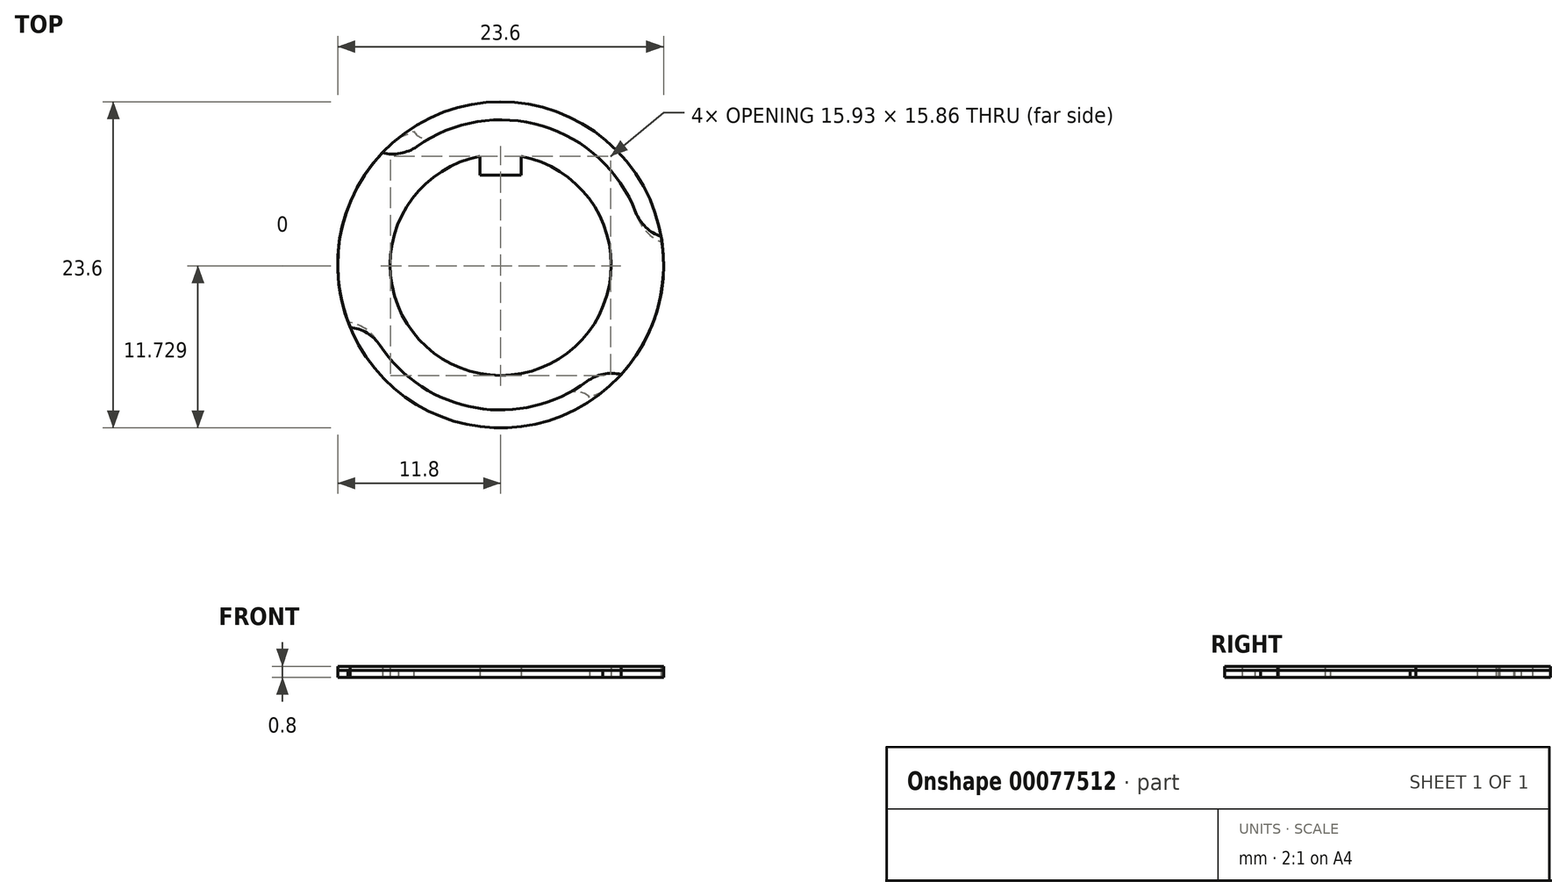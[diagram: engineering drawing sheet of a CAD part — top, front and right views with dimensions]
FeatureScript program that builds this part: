
annotation { "Feature Type Name" : "Feature", "Feature Type Description" : "" }
export const myFeature = defineFeature(function(context is Context, id is Id, definition is map)
    precondition{}
    {
        {
            var Q0;
            Q0=qCreatedBy(makeId("Top.planeOp"),FACE);
            var sketch = newSketch(context, id + "F0", { "sketchPlane" : qUnion([Q0])});
            skArc(sketch, "E0", {"start": v(7.4, -9.19) * mm, "mid": v(3.12, 11.38) * mm, "end": v(-11.05, -4.13) * mm});
            skArc(sketch, "E1", {"start": v(-1.5, 7.86) * mm, "mid": v(0, -8) * mm, "end": v(1.5, 7.86) * mm});
            skLineSegment(sketch, "E2", {"start": v(-1.5, 6.5) * mm, "end": v(1.5, 6.5) * mm});
            skPoint(sketch, "E3", {"position": v(0, 6.5) * mm});
            skLineSegment(sketch, "E4", {"start": v(1.5, 6.5) * mm, "end": v(1.5, 7.86) * mm});
            skLineSegment(sketch, "E5", {"start": v(-1.5, 6.5) * mm, "end": v(-1.5, 7.86) * mm});
            skLineSegment(sketch, "E6", {"start": v(0, 0) * mm, "end": v(6.6, -9.78) * mm, "construction": true});
            skLineSegment(sketch, "E7", {"start": v(0, 0) * mm, "end": v(-11.05, -4.13) * mm, "construction": true});
            skArc(sketch, "E8", {"start": v(-8.93, -5.52) * mm, "mid": v(-2.8, -10.12) * mm, "end": v(4.82, -9.33) * mm});
            skArc(sketch, "E9", {"start": v(-8.93, -5.52) * mm, "mid": v(-9.84, -4.6) * mm, "end": v(-11.05, -4.13) * mm});
            skArc(sketch, "E10", {"start": v(6.45, -9.6) * mm, "mid": v(5.68, -9.2) * mm, "end": v(4.82, -9.33) * mm});
            skLineSegment(sketch, "E11", {"start": v(7.4, -9.19) * mm, "end": v(6.45, -9.6) * mm});
            skSolve(sketch);
        }
        {
            var Q0;
            Q0=makeQuery(id+"F0.imprint","IMPRINT",FACE,{"disambiguationData":[TD([[makeQuery(id+"F0.imprint","IMPRINT",EDGE,{"derivedFrom":sQuery(id+"F0.wireOp",EDGE,"E0")}),1.0]])]});
            extrude(context, id + "F1", {"entities" : qUnion([Q0]), "depth" : 0.5 * mm});
        }
        {
            var Q0;
            Q0=qCreatedBy(makeId("Top.planeOp"),FACE);
            var sketch = newSketch(context, id + "F2", { "sketchPlane" : qUnion([Q0])});
            skArc(sketch, "E12", {"start": v(8.73, -7.93) * mm, "mid": v(2.02, 11.63) * mm, "end": v(-10.9, -4.52) * mm});
            skArc(sketch, "E13", {"start": v(-1.5, 7.86) * mm, "mid": v(0, -8) * mm, "end": v(1.5, 7.86) * mm});
            skLineSegment(sketch, "E14", {"start": v(-1.5, 6.5) * mm, "end": v(1.5, 6.5) * mm});
            skPoint(sketch, "E15", {"position": v(0, 6.5) * mm});
            skLineSegment(sketch, "E16", {"start": v(-1.5, 6.5) * mm, "end": v(-1.5, 7.86) * mm});
            skLineSegment(sketch, "E17", {"start": v(1.5, 6.5) * mm, "end": v(1.5, 7.86) * mm});
            skLineSegment(sketch, "E18", {"start": v(0, 0) * mm, "end": v(8.73, -7.93) * mm, "construction": true});
            skLineSegment(sketch, "E19", {"start": v(0, 0) * mm, "end": v(-10.9, -4.52) * mm, "construction": true});
            skArc(sketch, "E20", {"start": v(-8.73, -5.83) * mm, "mid": v(-1.8, -10.34) * mm, "end": v(6.25, -8.44) * mm});
            skArc(sketch, "E21", {"start": v(-8.73, -5.83) * mm, "mid": v(-9.67, -4.93) * mm, "end": v(-10.9, -4.52) * mm});
            skArc(sketch, "E22", {"start": v(8.73, -7.93) * mm, "mid": v(7.43, -7.91) * mm, "end": v(6.25, -8.44) * mm});
            skPoint(sketch, "E23.orphan", {"position": v(-9.7, -4.02) * mm});
            skPoint(sketch, "E24.orphan", {"position": v(7.77, -7.06) * mm});
            skSolve(sketch);
        }
        {
            var Q0;
            Q0=makeQuery(id+"F2.imprint","IMPRINT",FACE,{"disambiguationData":[TD([[makeQuery(id+"F2.imprint","IMPRINT",EDGE,{"derivedFrom":sQuery(id+"F2.wireOp",EDGE,"E12")}),1.0]])]});
            extrude(context, id + "F3", {"entities" : qUnion([Q0]), "depth" : 0.8 * mm});
        }
        {
            var Q0;
            Q0=qCreatedBy(makeId("Top.planeOp"),FACE);
            var sketch = newSketch(context, id + "F4", { "sketchPlane" : qUnion([Q0])});
            skArc(sketch, "E25", {"start": v(-1.5, 7.86) * mm, "mid": v(0, -8) * mm, "end": v(1.5, 7.86) * mm});
            skArc(sketch, "E26", {"start": v(-7.4, 9.19) * mm, "mid": v(-4.34, -10.97) * mm, "end": v(11.69, 1.64) * mm});
            skLineSegment(sketch, "E27", {"start": v(-1.5, 6.5) * mm, "end": v(1.5, 6.5) * mm});
            skPoint(sketch, "E28", {"position": v(0, 6.5) * mm});
            skLineSegment(sketch, "E29", {"start": v(-1.5, 6.5) * mm, "end": v(-1.5, 7.86) * mm});
            skLineSegment(sketch, "E30", {"start": v(1.5, 6.5) * mm, "end": v(1.5, 7.86) * mm});
            skLineSegment(sketch, "E31", {"start": v(0, 0) * mm, "end": v(-6.38, 9.92) * mm, "construction": true});
            skLineSegment(sketch, "E32", {"start": v(0, 0) * mm, "end": v(11.69, 1.64) * mm, "construction": true});
            skArc(sketch, "E33", {"start": v(9.91, 3.46) * mm, "mid": v(3.82, 9.78) * mm, "end": v(-4.94, 9.27) * mm});
            skArc(sketch, "E34", {"start": v(-6.28, 9.66) * mm, "mid": v(-5.7, 9.19) * mm, "end": v(-4.94, 9.27) * mm});
            skArc(sketch, "E35", {"start": v(9.91, 3.46) * mm, "mid": v(10.6, 2.35) * mm, "end": v(11.69, 1.64) * mm});
            skLineSegment(sketch, "E36", {"start": v(-7.4, 9.19) * mm, "end": v(-6.28, 9.66) * mm});
            skSolve(sketch);
        }
        {
            var Q0;
            Q0=makeQuery(id+"F4.imprint","IMPRINT",FACE,{"disambiguationData":[TD([[makeQuery(id+"F4.imprint","IMPRINT",EDGE,{"derivedFrom":sQuery(id+"F4.wireOp",EDGE,"E25")}),-1.0]])]});
            extrude(context, id + "F5", {"entities" : qUnion([Q0]), "depth" : 0.5 * mm});
        }
        {
            var Q0;
            Q0=qCreatedBy(makeId("Top.planeOp"),FACE);
            var sketch = newSketch(context, id + "F6", { "sketchPlane" : qUnion([Q0])});
            skArc(sketch, "E37", {"start": v(-1.5, 7.86) * mm, "mid": v(0, -8) * mm, "end": v(1.5, 7.86) * mm});
            skArc(sketch, "E38", {"start": v(-8.56, 8.12) * mm, "mid": v(-3.4, -11.3) * mm, "end": v(11.62, 2.05) * mm});
            skLineSegment(sketch, "E39", {"start": v(-1.5, 6.5) * mm, "end": v(1.5, 6.5) * mm});
            skPoint(sketch, "E40", {"position": v(0, 6.5) * mm});
            skLineSegment(sketch, "E41", {"start": v(-1.5, 6.5) * mm, "end": v(-1.5, 7.86) * mm});
            skLineSegment(sketch, "E42", {"start": v(1.5, 6.5) * mm, "end": v(1.5, 7.86) * mm});
            skLineSegment(sketch, "E43", {"start": v(0, 0) * mm, "end": v(-8.56, 8.12) * mm, "construction": true});
            skLineSegment(sketch, "E44", {"start": v(0, 0) * mm, "end": v(11.62, 2.05) * mm, "construction": true});
            skArc(sketch, "E45", {"start": v(9.79, 3.8) * mm, "mid": v(3.03, 10.05) * mm, "end": v(-6.06, 8.57) * mm});
            skArc(sketch, "E46", {"start": v(-8.56, 8.12) * mm, "mid": v(-7.26, 8.07) * mm, "end": v(-6.06, 8.57) * mm});
            skArc(sketch, "E47", {"start": v(9.79, 3.8) * mm, "mid": v(10.5, 2.72) * mm, "end": v(11.62, 2.05) * mm});
            skSolve(sketch);
        }
        {
            var Q0;
            Q0=makeQuery(id+"F6.imprint","IMPRINT",FACE,{"disambiguationData":[TD([[makeQuery(id+"F6.imprint","IMPRINT",EDGE,{"derivedFrom":sQuery(id+"F6.wireOp",EDGE,"E37")}),-1.0]])]});
            extrude(context, id + "F7", {"entities" : qUnion([Q0]), "depth" : 0.8 * mm});
        }
    });
